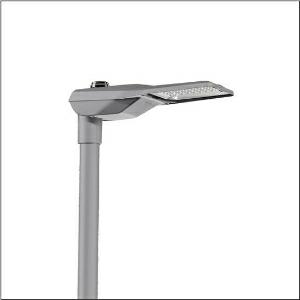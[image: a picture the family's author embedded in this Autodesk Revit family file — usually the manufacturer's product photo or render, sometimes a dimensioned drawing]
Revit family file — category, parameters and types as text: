
# Revit family: streetlight_sl_21_mini___st1_0a_5xe6d57n08hb_5f9a
name_source: partatom
category: Lighting Fixtures
units: mm (PartAtom-declared; Revit-internal decimal feet)

## family parameters
Cut with Voids When Loaded = No
Host = Face
Light Source = No
Part Type = Normal
Room Calculation Point = No
Round Connector Dimension = Use Diameter
Shared = No

## types (1)
- --- (1 x LED, 7780 lm, 66 W, 3000K)
    Apparent Load = 66 VA
    CIE Flux Codes = 37 72 97 100 100
    Color Rendering = 80
    Color Temperature = 3000K
    Default Elevation = 1800 mm
    Description = Streetlight SL 21 mini, mast luminaire, primary light control with lens, of PMMA, primary optical cover: cover, of toughened safety glass, transparent, light distribution: ST1.0a, light emission: direct distribution, primary light characteristic: asymmetric, installation type: side-entry, LED, 3G 1.5mm², High Power LED, rated luminous flux: 7.780lm, luminous efficacy: 118lm/W, light colour: 830, colour temperature: 3000K, control gear: NEMA (7pin), control: overheat protection, pre-setting: linear dimming characteristic, constant luminous flux control, time-dependent luminous flux control, flexible luminous flux parameterisation, mains connection: 230..240V, AC, 50/60Hz, connection cable pre-assembled, cable length: 8,5m, wiring characteristics: H07RN-F, start of lifetime: 66W, end of service life: 69W, reduction: 30W, luminaire housing, of diecast aluminium (EN AC-44300), powder-coated, Siteco® metallic grey (DB 702S), corrosivity category C5 mid according to DIN EN ISO 12944, multi-level sealing system, sealing non-destructively replaceable, inclination adjustable: 0°, 5°, 10°, 15°, length: 628mm, width: 235mm, height: 110mm, spigot size: 42mm (side-entry), mounting height: 4..8m, protection rating (complete): IP66, insulation class (complete): insulation class I (protective earthing), certification: CE, ENEC, ENEC+, VDE, impact resistance: IK10, permissible operating ambient temperature for outdoor applications: -40..+50°C, standard-compliant lighting for roads and squares, packaging unit: 1 piece

Light Distribution: ST1.0a
    Height = 110 mm
    Lamp = 1 x LED
    Lamp Light Flux = 7780 lm
    Lamp Power = 66 W
    Lamp count = 1
    Length = 625 mm
    Luminous efficacy = 118 lm/W
    Manufacturer = Siteco
    ModVariant = No
    Model = 5XE6D57N08HB
    Number of Poles = 1
    OnlyDefault = Yes
    Power Factor = 1
    Product Name = Streetlight SL 21 mini | ST1.0a
    Product group = mast luminaire | pylon top
    ProductGroupID = 6100
    Protection Class = Protection class I
    Protection Degree = IP 66
    RLX_Detail_Level = 1
    RLX_Emergency_Light_Flux = 0 lm
    RLX_Emergency_Type = 0
    RLX_Emergency_Type_DB = No
    RlxData = <blob elided: 26137 chars, md5=78cdc58f>
    Socket = socket
    Standby Power = 0 W
    System Light Flux = 7780 lm
    System Power = 66 W
    Type Comments = factory setting: luminous flux: 100 % | dim-lin: 254 | 670 mA
    Type Image = l_1294379.jpg
    URL = http://relux.com
    VarID = @adj_157643
    Voltage = 0 V
    Weight = 0.00 kg
    Width = 234 mm

## geometry (parser evidence)
native form markers: Blend x4, Sweep x11
no freeform markers — native parametric forms only
